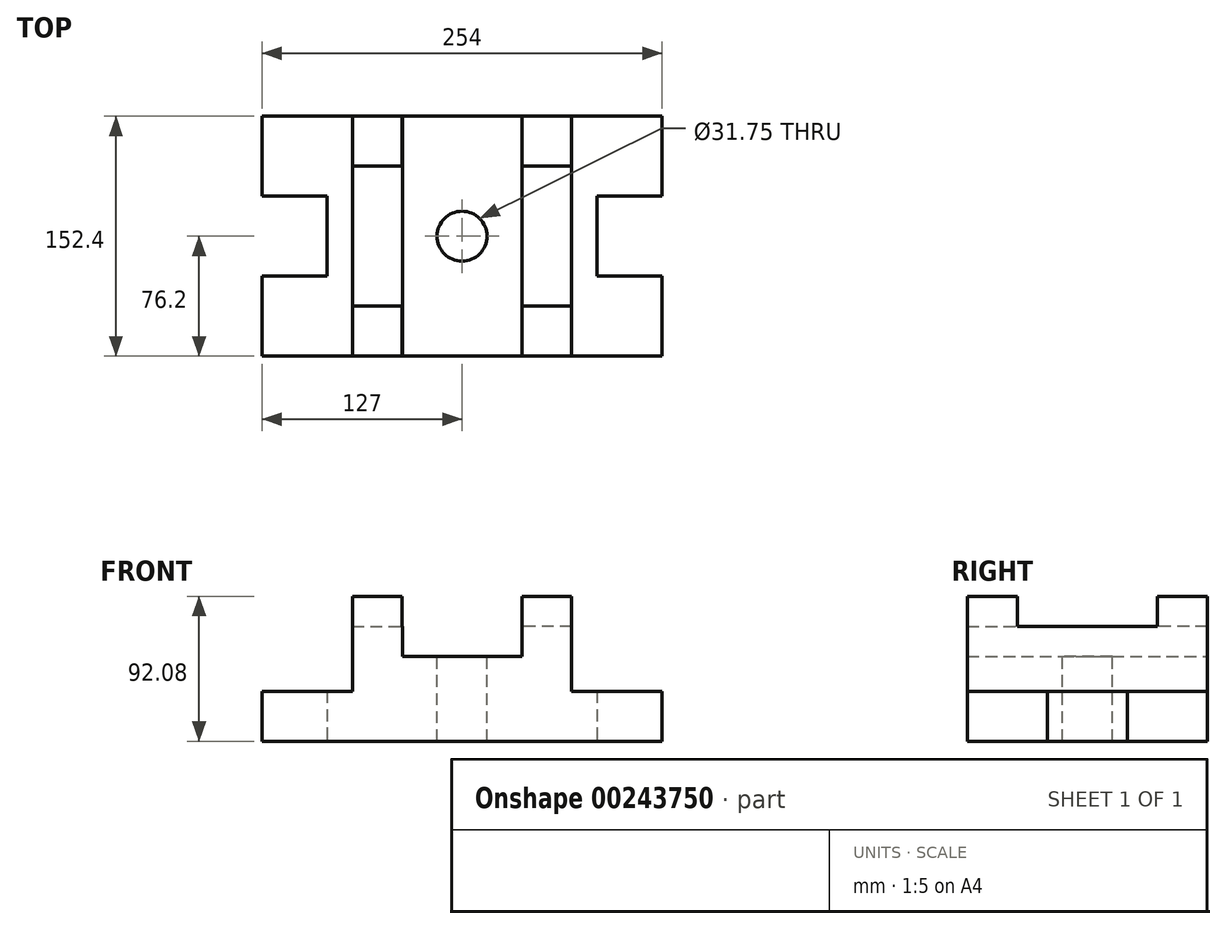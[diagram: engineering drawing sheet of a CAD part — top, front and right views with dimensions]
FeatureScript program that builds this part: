
annotation { "Feature Type Name" : "Feature", "Feature Type Description" : "" }
export const myFeature = defineFeature(function(context is Context, id is Id, definition is map)
    precondition{}
    {
        {
            var Q0;
            Q0=qCreatedBy(makeId("Top.planeOp"),FACE);
            var sketch = newSketch(context, id + "F0", { "sketchPlane" : qUnion([Q0])});
            skLineSegment(sketch, "E0.bottom", {"start": v(127, 76.2) * mm, "end": v(-127, 76.2) * mm});
            skLineSegment(sketch, "E0.top", {"start": v(127, -76.2) * mm, "end": v(-127, -76.2) * mm});
            skLineSegment(sketch, "E0.left", {"start": v(127, 76.2) * mm, "end": v(127, 25.4) * mm});
            skLineSegment(sketch, "E0.right", {"start": v(-127, 76.2) * mm, "end": v(-127, 25.4) * mm});
            skPoint(sketch, "E0.middle", {"position": v(0, 0) * mm});
            skLineSegment(sketch, "E1.bottom", {"start": v(-127, 25.4) * mm, "end": v(-85.73, 25.4) * mm});
            skLineSegment(sketch, "E1.top", {"start": v(-127, -25.4) * mm, "end": v(-85.73, -25.4) * mm});
            skLineSegment(sketch, "E1.right", {"start": v(-85.73, 25.4) * mm, "end": v(-85.73, -25.4) * mm});
            skLineSegment(sketch, "E2", {"start": v(0, 76.2) * mm, "end": v(0, -76.2) * mm});
            skLineSegment(sketch, "E3.MirrorCS", {"start": v(127, 25.4) * mm, "end": v(85.72, 25.4) * mm});
            skLineSegment(sketch, "E4.MirrorCS", {"start": v(85.73, 25.4) * mm, "end": v(85.72, -25.4) * mm});
            skLineSegment(sketch, "E5.MirrorCS", {"start": v(127, -25.4) * mm, "end": v(85.72, -25.4) * mm});
            skLineSegment(sketch, "E6.trimOffspring", {"start": v(-127, -25.4) * mm, "end": v(-127, -76.2) * mm});
            skLineSegment(sketch, "E7.trimOffspring", {"start": v(127, -25.4) * mm, "end": v(127, -76.2) * mm});
            skSolve(sketch);
        }
        {
            var Q0;
            {var subQ1=sQuery(id+"F0.wireOp",EDGE,"E0.right");Q0=makeQuery(id+"F0.imprint","IMPRINT",FACE,{"disambiguationData":[TD([[makeQuery(id+"F0.imprint","IMPRINT",EDGE,{"derivedFrom":subQ1}),1.0]])]});}
            var Q1;
            {var subQ3=sQuery(id+"F0.wireOp",EDGE,"E0.left");Q1=makeQuery(id+"F0.imprint","IMPRINT",FACE,{"disambiguationData":[TD([[makeQuery(id+"F0.imprint","IMPRINT",EDGE,{"derivedFrom":subQ3}),-1.0]])]});}
            extrude(context, id + "F1", {"entities" : qUnion([Q0, Q1]), "depth" : 31.75 * mm});
        }
        {
            var Q0;
            Q0=makeQuery(id+"F1.opExtrude","CAP_FACE",FACE,{"disambiguationData":[OSD([sQuery(id+"F0.wireOp",EDGE,"E0.bottom"),sQuery(id+"F0.wireOp",EDGE,"E0.top"),sQuery(id+"F0.wireOp",EDGE,"E0.left"),sQuery(id+"F0.wireOp",EDGE,"E0.right"),sQuery(id+"F0.wireOp",EDGE,"E1.bottom"),sQuery(id+"F0.wireOp",EDGE,"E1.top"),sQuery(id+"F0.wireOp",EDGE,"E1.right"),sQuery(id+"F0.wireOp",EDGE,"E3.MirrorCS"),sQuery(id+"F0.wireOp",EDGE,"E4.MirrorCS"),sQuery(id+"F0.wireOp",EDGE,"E5.MirrorCS"),sQuery(id+"F0.wireOp",EDGE,"E6.trimOffspring"),sQuery(id+"F0.wireOp",EDGE,"E7.trimOffspring")])],"isStart":false});
            var sketch = newSketch(context, id + "F2", { "sketchPlane" : qUnion([Q0])});
            skLineSegment(sketch, "E8.bottom", {"start": v(-69.65, 76.2) * mm, "end": v(70.05, 76.2) * mm});
            skLineSegment(sketch, "E8.top", {"start": v(-69.65, -76.2) * mm, "end": v(70.05, -76.2) * mm});
            skLineSegment(sketch, "E8.left", {"start": v(-69.65, 76.2) * mm, "end": v(-69.65, -76.2) * mm});
            skLineSegment(sketch, "E8.right", {"start": v(70.05, 76.2) * mm, "end": v(70.05, -76.2) * mm});
            skLineSegment(sketch, "E9", {"start": v(0, 76.2) * mm, "end": v(0, -76.2) * mm});
            skLineSegment(sketch, "E10.MirrorCS", {"start": v(69.65, 76.2) * mm, "end": v(69.65, -76.2) * mm});
            skLineSegment(sketch, "E11.MirrorCS", {"start": v(-70.05, 76.2) * mm, "end": v(-70.05, -76.2) * mm});
            skSolve(sketch);
        }
        {
            var Q0;
            {var subQ0=sQuery(id+"F2.wireOp",EDGE,"E9");Q0=makeQuery(id+"F2.imprint","IMPRINT",FACE,{"disambiguationData":[TD([[makeQuery(id+"F2.imprint","IMPRINT",EDGE,{"derivedFrom":subQ0}),1.0]])]});}
            var Q1;
            {var subQ0=sQuery(id+"F2.wireOp",EDGE,"E8.left");Q1=makeQuery(id+"F2.imprint","IMPRINT",FACE,{"disambiguationData":[TD([[makeQuery(id+"F2.imprint","IMPRINT",EDGE,{"derivedFrom":subQ0}),1.0]])]});}
            extrude(context, id + "F3", {"entities" : qUnion([Q0, Q1]), "operationType" : NewBodyOperationType.ADD, "depth" : 22.22 * mm});
        }
        {
            var Q0;
            Q0=makeQuery(id+"F3.opExtrude","CAP_FACE",FACE,{"disambiguationData":[OSD([sQuery(id+"F2.wireOp",EDGE,"E8.bottom"),sQuery(id+"F2.wireOp",EDGE,"E8.top"),sQuery(id+"F2.wireOp",EDGE,"E8.left"),sQuery(id+"F2.wireOp",EDGE,"E10.MirrorCS")])],"isStart":false});
            var sketch = newSketch(context, id + "F4", { "sketchPlane" : qUnion([Q0])});
            skLineSegment(sketch, "E12", {"start": v(0, 76.2) * mm, "end": v(0, -76.2) * mm});
            skLineSegment(sketch, "E13.top", {"start": v(-69.85, -76.2) * mm, "end": v(-38.1, -76.2) * mm});
            skLineSegment(sketch, "E13.left", {"start": v(-69.85, 76.2) * mm, "end": v(-69.85, -76.2) * mm});
            skLineSegment(sketch, "E14.MirrorCS", {"start": v(38.1, 76.2) * mm, "end": v(38.1, -76.2) * mm});
            skPoint(sketch, "E15.MirrorCS.end.orphan", {"position": v(69.85, -76.2) * mm});
            skPoint(sketch, "E15.MirrorCS.start.orphan", {"position": v(69.85, 76.2) * mm});
            skLineSegment(sketch, "E16.bottom", {"start": v(38.1, 76.2) * mm, "end": v(69.85, 76.2) * mm});
            skLineSegment(sketch, "E16.top", {"start": v(38.1, -76.2) * mm, "end": v(69.85, -76.2) * mm});
            skLineSegment(sketch, "E16.right", {"start": v(69.85, 76.2) * mm, "end": v(69.85, -76.2) * mm});
            skLineSegment(sketch, "E17.bottom", {"start": v(-69.65, -76.2) * mm, "end": v(-37.9, -76.2) * mm});
            skLineSegment(sketch, "E17.top", {"start": v(-69.65, 76.2) * mm, "end": v(-37.9, 76.2) * mm});
            skLineSegment(sketch, "E17.left", {"start": v(-69.65, -76.2) * mm, "end": v(-69.65, 76.2) * mm});
            skLineSegment(sketch, "E17.right", {"start": v(-37.9, -76.2) * mm, "end": v(-37.9, 76.2) * mm});
            skSolve(sketch);
        }
        {
            var Q0;
            Q0=makeQuery(id+"F4.imprint","IMPRINT",FACE,{"disambiguationData":[TD([[makeQuery(id+"F4.imprint","IMPRINT",EDGE,{"derivedFrom":sQuery(id+"F4.wireOp",EDGE,"E13.bottom")}),1.0]])]});
            var Q1;
            {var subQ0=sQuery(id+"F4.wireOp",EDGE,"E14.MirrorCS");Q1=makeQuery(id+"F4.imprint","IMPRINT",FACE,{"disambiguationData":[TD([[makeQuery(id+"F4.imprint","IMPRINT",EDGE,{"derivedFrom":subQ0}),1.0]])]});}
            extrude(context, id + "F5", {"entities" : qUnion([Q0, Q1]), "operationType" : NewBodyOperationType.ADD, "depth" : 19.05 * mm});
        }
        {
            var Q0;
            Q0=makeQuery(id+"F5.opExtrude","CAP_FACE",FACE,{"disambiguationData":[OSD([sQuery(id+"F2.wireOp",EDGE,"E8.bottom"),sQuery(id+"F2.wireOp",EDGE,"E8.top"),sQuery(id+"F4.wireOp",EDGE,"E14.MirrorCS"),sQuery(id+"F4.wireOp",EDGE,"E15.MirrorCS")])],"isStart":false});
            var sketch = newSketch(context, id + "F6", { "sketchPlane" : qUnion([Q0])});
            skLineSegment(sketch, "E18.bottom", {"start": v(69.65, -76.2) * mm, "end": v(38.1, -76.2) * mm});
            skLineSegment(sketch, "E18.top", {"start": v(69.65, -44.45) * mm, "end": v(38.1, -44.45) * mm});
            skLineSegment(sketch, "E18.left", {"start": v(69.65, -76.2) * mm, "end": v(69.65, -44.45) * mm});
            skLineSegment(sketch, "E18.right", {"start": v(38.1, -76.2) * mm, "end": v(38.1, -44.45) * mm});
            skLineSegment(sketch, "E19", {"start": v(0, -74.54) * mm, "end": v(0, 76.56) * mm});
            skLineSegment(sketch, "E20", {"start": v(-70.22, 0) * mm, "end": v(69.65, 0) * mm});
            skLineSegment(sketch, "E21.MirrorCS", {"start": v(0, 74.54) * mm, "end": v(0, -76.56) * mm});
            skLineSegment(sketch, "E22.MirrorCS", {"start": v(-69.65, -44.45) * mm, "end": v(-38.1, -44.45) * mm});
            skLineSegment(sketch, "E23.MirrorCS", {"start": v(-38.1, -76.2) * mm, "end": v(-38.1, -44.45) * mm});
            skLineSegment(sketch, "E24.MirrorCS", {"start": v(-69.65, -76.2) * mm, "end": v(-38.1, -76.2) * mm});
            skLineSegment(sketch, "E25.MirrorCS", {"start": v(-69.65, -76.2) * mm, "end": v(-69.65, -44.45) * mm});
            skLineSegment(sketch, "E26.MirrorCS", {"start": v(-69.65, 44.45) * mm, "end": v(-38.1, 44.45) * mm});
            skLineSegment(sketch, "E27.MirrorCS", {"start": v(-69.65, 76.2) * mm, "end": v(-69.65, 44.45) * mm});
            skLineSegment(sketch, "E28.MirrorCS", {"start": v(-38.1, 76.2) * mm, "end": v(-38.1, 44.45) * mm});
            skLineSegment(sketch, "E29.MirrorCS", {"start": v(-69.65, 76.2) * mm, "end": v(-38.1, 76.2) * mm});
            skLineSegment(sketch, "E30.MirrorCS", {"start": v(69.65, 44.45) * mm, "end": v(38.1, 44.45) * mm});
            skLineSegment(sketch, "E31.MirrorCS", {"start": v(38.1, 76.2) * mm, "end": v(38.1, 44.45) * mm});
            skLineSegment(sketch, "E32.MirrorCS", {"start": v(69.65, 76.2) * mm, "end": v(38.1, 76.2) * mm});
            skLineSegment(sketch, "E33.MirrorCS", {"start": v(69.65, 76.2) * mm, "end": v(69.65, 44.45) * mm});
            skSolve(sketch);
        }
        {
            var Q0;
            Q0 = qSketchRegion(id + "F6", true);
            extrude(context, id + "F7", {"entities" : qUnion([Q0]), "operationType" : NewBodyOperationType.ADD, "depth" : 19.05 * mm});
        }
        {
            var Q0;
            Q0=makeQuery(id+"F3.opExtrude","CAP_FACE",FACE,{"disambiguationData":[OSD([sQuery(id+"F2.wireOp",EDGE,"E8.bottom"),sQuery(id+"F2.wireOp",EDGE,"E8.top"),sQuery(id+"F2.wireOp",EDGE,"E8.left"),sQuery(id+"F2.wireOp",EDGE,"E10.MirrorCS")])],"isStart":false});
            var sketch = newSketch(context, id + "F8", { "sketchPlane" : qUnion([Q0])});
            skCircle(sketch, "E34", {"center": v(0, 0) * mm, "radius": 15.88 * mm});
            skSolve(sketch);
        }
        {
            var Q0;
            Q0=sQuery(id+"F8.wireOp",VERTEX,"E34.center");
            var Q1;
            Q1=makeQuery(id+"F1.opExtrude","SWEPT_BODY",BODY,{"disambiguationData":[OSD([sQuery(id+"F0.wireOp",EDGE,"E0.bottom"),sQuery(id+"F0.wireOp",EDGE,"E0.top"),sQuery(id+"F0.wireOp",EDGE,"E0.left"),sQuery(id+"F0.wireOp",EDGE,"E0.right"),sQuery(id+"F0.wireOp",EDGE,"E1.bottom"),sQuery(id+"F0.wireOp",EDGE,"E1.top"),sQuery(id+"F0.wireOp",EDGE,"E1.right"),sQuery(id+"F0.wireOp",EDGE,"E3.MirrorCS"),sQuery(id+"F0.wireOp",EDGE,"E4.MirrorCS"),sQuery(id+"F0.wireOp",EDGE,"E5.MirrorCS"),sQuery(id+"F0.wireOp",EDGE,"E6.trimOffspring"),sQuery(id+"F0.wireOp",EDGE,"E7.trimOffspring")])]});
            hole(context, id + "F9", {"style" : HoleStyle.SIMPLE, "endStyle" : HoleEndStyle.THROUGH, "holeDiameter" : 31.75 * mm, "locations" : qUnion([Q0]), "scope" : qUnion([Q1]), "isTappedThrough" : true});
        }
        {
            var Q0;
            Q0=makeQuery(id+"F6.imprint","IMPRINT",FACE,{"disambiguationData":[TD([[makeQuery(id+"F6.imprint","IMPRINT",EDGE,{"derivedFrom":sQuery(id+"F6.wireOp",EDGE,"E30.MirrorCS")}),-1.0]])]});
            var Q1;
            Q1=makeQuery(id+"F6.imprint","IMPRINT",FACE,{"disambiguationData":[TD([[makeQuery(id+"F6.imprint","IMPRINT",EDGE,{"derivedFrom":sQuery(id+"F6.wireOp",EDGE,"E26.MirrorCS")}),1.0]])]});
            var Q2;
            Q2=makeQuery(id+"F6.imprint","IMPRINT",FACE,{"disambiguationData":[TD([[makeQuery(id+"F6.imprint","IMPRINT",EDGE,{"derivedFrom":sQuery(id+"F6.wireOp",EDGE,"E22.MirrorCS")}),-1.0]])]});
            var Q3;
            Q3=makeQuery(id+"F6.imprint","IMPRINT",FACE,{"disambiguationData":[TD([[makeQuery(id+"F6.imprint","IMPRINT",EDGE,{"derivedFrom":sQuery(id+"F6.wireOp",EDGE,"E18.bottom")}),-1.0]])]});
            extrude(context, id + "F10", {"entities" : qUnion([Q0, Q1, Q2, Q3]), "operationType" : NewBodyOperationType.ADD, "depth" : 19.05 * mm});
        }
        {
            var Q0;
            {var subQ2=sQuery(id+"F4.wireOp",EDGE,"E14.MirrorCS");Q0=makeQuery(id+"F4.imprint","IMPRINT",FACE,{"disambiguationData":[TD([[makeQuery(id+"F4.imprint","IMPRINT",EDGE,{"derivedFrom":subQ2}),1.0]])]});}
            extrude(context, id + "F11", {"entities" : qUnion([Q0]), "operationType" : NewBodyOperationType.ADD, "depth" : 19.05 * mm});
        }
        {
            var Q0;
            Q0=makeQuery(id+"F4.imprint","IMPRINT",FACE,{"disambiguationData":[TD([[makeQuery(id+"F4.imprint","IMPRINT",EDGE,{"derivedFrom":sQuery(id+"F4.wireOp",EDGE,"E17.top")}),1.0]])]});
            extrude(context, id + "F12", {"entities" : qUnion([Q0]), "operationType" : NewBodyOperationType.ADD, "depth" : 19.05 * mm});
        }
    });
